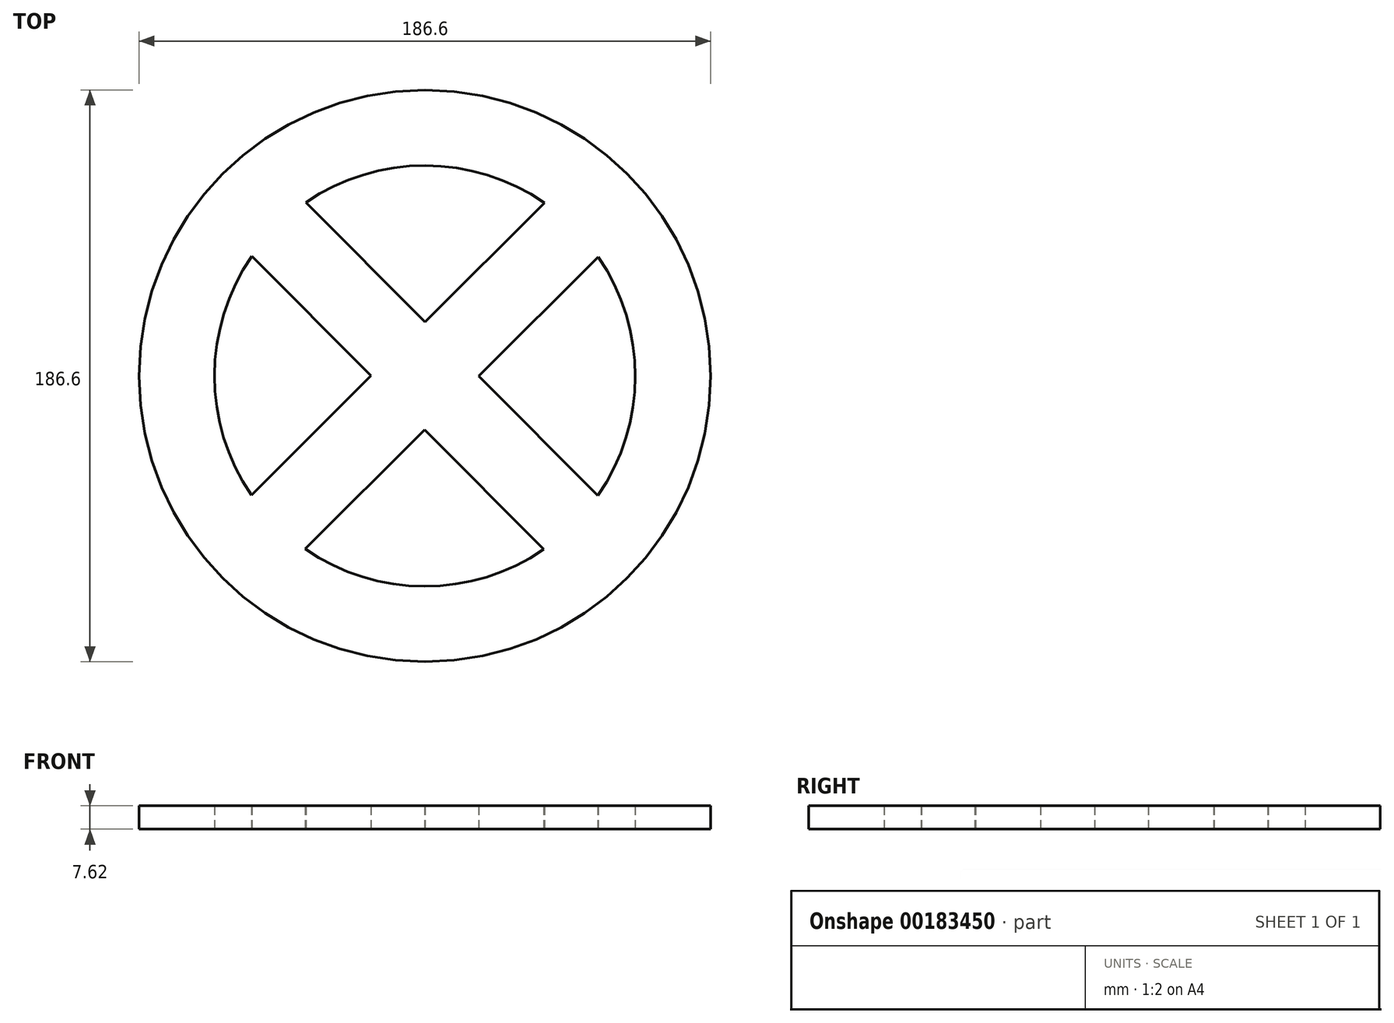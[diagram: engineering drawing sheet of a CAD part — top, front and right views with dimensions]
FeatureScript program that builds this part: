
annotation { "Feature Type Name" : "Feature", "Feature Type Description" : "" }
export const myFeature = defineFeature(function(context is Context, id is Id, definition is map)
    precondition{}
    {
        {
            var Q0;
            Q0=qCreatedBy(makeId("Top.planeOp"),FACE);
            var sketch = newSketch(context, id + "F0", { "sketchPlane" : qUnion([Q0])});
            skArc(sketch, "E0", {"start": v(-56.48, 39.05) * mm, "mid": v(-68.66, 0.13) * mm, "end": v(-56.62, -38.84) * mm});
            skCircle(sketch, "E1.0", {"center": v(0, 0) * mm, "radius": 93.3 * mm});
            skLineSegment(sketch, "E2.0", {"start": v(0.03, 17.6) * mm, "end": v(-38.84, 56.62) * mm});
            skLineSegment(sketch, "E3.0", {"start": v(-17.6, 0.03) * mm, "end": v(-56.48, 39.05) * mm});
            skLineSegment(sketch, "E4.0", {"start": v(0.03, 17.6) * mm, "end": v(39.05, 56.48) * mm});
            skLineSegment(sketch, "E5.0", {"start": v(17.6, -0.03) * mm, "end": v(56.62, 38.84) * mm});
            skArc(sketch, "E6.trimOffspring", {"start": v(39.05, 56.48) * mm, "mid": v(0.13, 68.66) * mm, "end": v(-38.84, 56.62) * mm});
            skLineSegment(sketch, "E7.0", {"start": v(-17.6, 0.03) * mm, "end": v(-56.62, -38.84) * mm});
            skLineSegment(sketch, "E8.0", {"start": v(-0.03, -17.6) * mm, "end": v(-39.05, -56.48) * mm});
            skLineSegment(sketch, "E9.0", {"start": v(-0.03, -17.6) * mm, "end": v(38.84, -56.62) * mm});
            skLineSegment(sketch, "E10.0", {"start": v(17.6, -0.03) * mm, "end": v(56.48, -39.05) * mm});
            skArc(sketch, "E11.trimOffspring", {"start": v(-39.05, -56.48) * mm, "mid": v(-0.13, -68.66) * mm, "end": v(38.84, -56.62) * mm});
            skArc(sketch, "E12.trimOffspring", {"start": v(56.48, -39.05) * mm, "mid": v(68.66, -0.13) * mm, "end": v(56.62, 38.84) * mm});
            skSolve(sketch);
        }
        {
            var Q0;
            Q0=makeQuery(id+"F0.imprint","IMPRINT",FACE,{"disambiguationData":[TD([[makeQuery(id+"F0.imprint","IMPRINT",EDGE,{"derivedFrom":sQuery(id+"F0.wireOp",EDGE,"E0")}),-1.0]])]});
            extrude(context, id + "F1", {"entities" : qUnion([Q0]), "depth" : 7.62 * mm});
        }
    });
